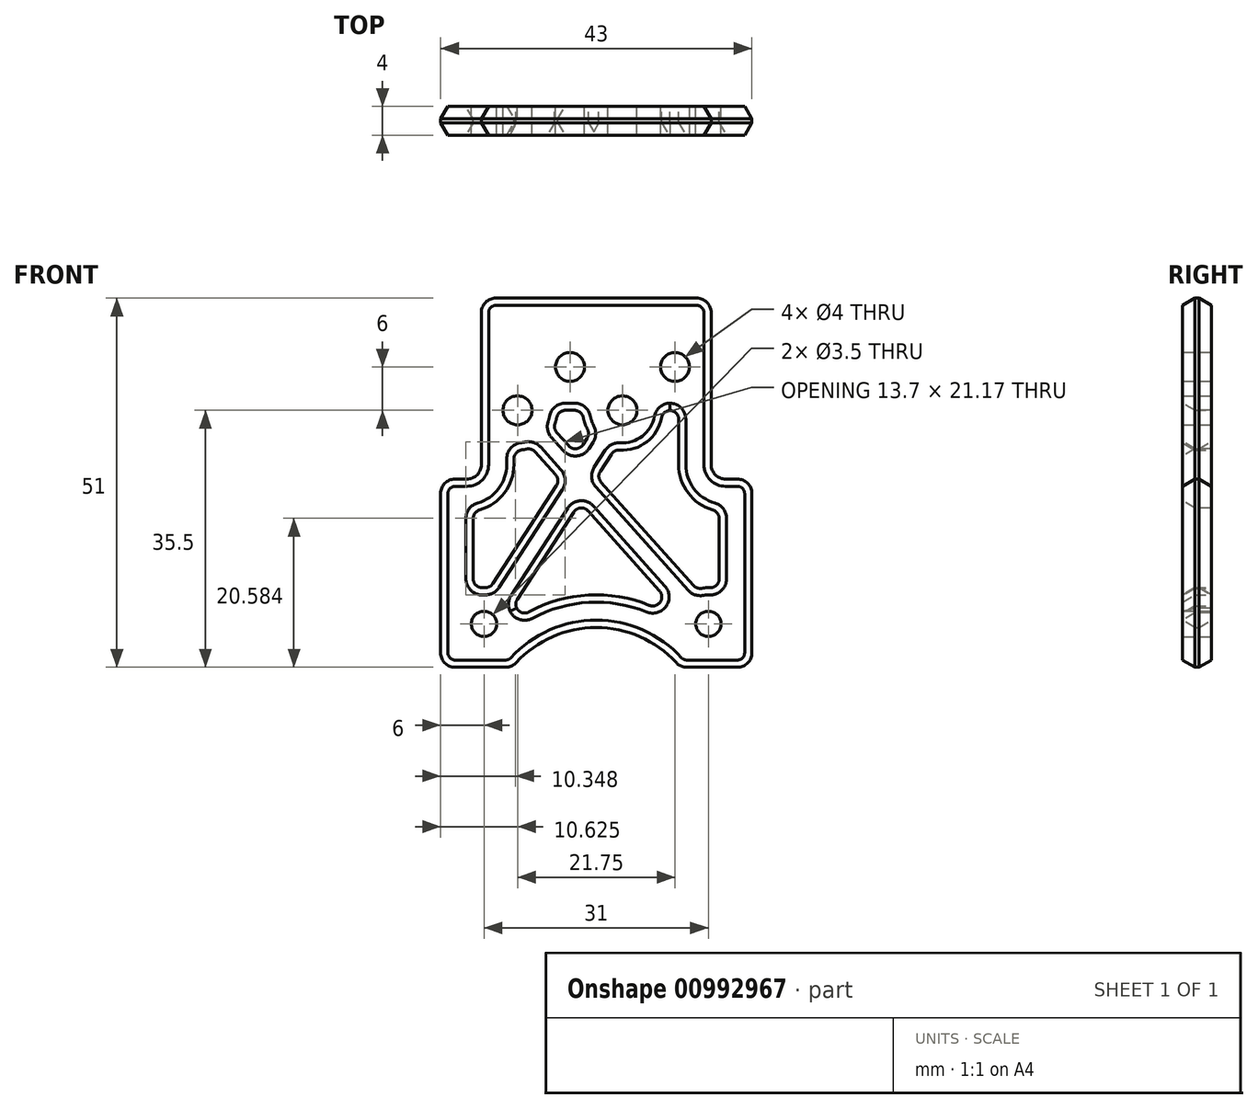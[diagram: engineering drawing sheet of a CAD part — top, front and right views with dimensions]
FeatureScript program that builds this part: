
annotation { "Feature Type Name" : "Feature", "Feature Type Description" : "" }
export const myFeature = defineFeature(function(context is Context, id is Id, definition is map)
    precondition{}
    {
        {
            var Q0;
            Q0=qCreatedBy(makeId("Front.planeOp"),FACE);
            var sketch = newSketch(context, id + "F0", { "sketchPlane" : qUnion([Q0])});
            skCircle(sketch, "E0", {"center": v(0, 0) * mm, "radius": 21.92 * mm, "construction": true});
            skLineSegment(sketch, "E1.bottom", {"start": v(-15.5, 15.5) * mm, "end": v(15.5, 15.5) * mm, "construction": true});
            skLineSegment(sketch, "E1.top", {"start": v(-15.5, -15.5) * mm, "end": v(15.5, -15.5) * mm, "construction": true});
            skLineSegment(sketch, "E1.left", {"start": v(-15.5, 15.5) * mm, "end": v(-15.5, -15.5) * mm, "construction": true});
            skLineSegment(sketch, "E1.right", {"start": v(15.5, 15.5) * mm, "end": v(15.5, -15.5) * mm, "construction": true});
            skCircle(sketch, "E2", {"center": v(-15.5, 15.5) * mm, "radius": 1.75 * mm});
            skCircle(sketch, "E3", {"center": v(15.5, 15.5) * mm, "radius": 1.75 * mm});
            skArc(sketch, "E4", {"start": v(11.6, 9.5) * mm, "mid": v(0, 15) * mm, "end": v(-11.6, 9.5) * mm});
            skLineSegment(sketch, "E5", {"start": v(-11.6, 9.5) * mm, "end": v(-21.5, 9.5) * mm});
            skLineSegment(sketch, "E6", {"start": v(-21.5, 9.5) * mm, "end": v(-21.5, 33.5) * mm});
            skLineSegment(sketch, "E7", {"start": v(-13.88, 60.5) * mm, "end": v(13.88, 60.5) * mm});
            skLineSegment(sketch, "E8", {"start": v(21.5, 33.5) * mm, "end": v(21.5, 9.5) * mm});
            skLineSegment(sketch, "E9", {"start": v(21.5, 9.5) * mm, "end": v(11.6, 9.5) * mm});
            skLineSegment(sketch, "E10", {"start": v(-21.5, 35.5) * mm, "end": v(21.5, 35.5) * mm, "construction": true});
            skPoint(sketch, "E10.endSnap0", {"position": v(21.5, 35) * mm});
            skLineSegment(sketch, "E11", {"start": v(15.88, 51) * mm, "end": v(-15.88, 51) * mm, "construction": true});
            skLineSegment(sketch, "E12", {"start": v(15.88, 45) * mm, "end": v(-15.88, 45) * mm, "construction": true});
            skLineSegment(sketch, "E13", {"start": v(15.88, 48) * mm, "end": v(-15.88, 48) * mm, "construction": true});
            skCircle(sketch, "E14", {"center": v(10.88, 51) * mm, "radius": 2 * mm});
            skCircle(sketch, "E15", {"center": v(3.63, 45) * mm, "radius": 2 * mm});
            skCircle(sketch, "E16", {"center": v(-10.88, 45) * mm, "radius": 2 * mm});
            skCircle(sketch, "E17", {"center": v(-3.62, 51) * mm, "radius": 2 * mm});
            skLineSegment(sketch, "E18", {"start": v(-3.63, 51) * mm, "end": v(3.63, 45) * mm, "construction": true});
            skLineSegment(sketch, "E19", {"start": v(0, -0.66) * mm, "end": v(0, 48) * mm, "construction": true});
            skLineSegment(sketch, "E20", {"start": v(-19.5, 35.5) * mm, "end": v(-15.87, 35.5) * mm});
            skLineSegment(sketch, "E21", {"start": v(-15.87, 35.5) * mm, "end": v(-15.88, 58.5) * mm});
            skLineSegment(sketch, "E22", {"start": v(19.5, 35.5) * mm, "end": v(15.88, 35.5) * mm});
            skLineSegment(sketch, "E23", {"start": v(15.88, 35.5) * mm, "end": v(15.88, 58.5) * mm});
            skPoint(sketch, "E24.orphan", {"position": v(21.5, 60.5) * mm});
            skCircle(sketch, "E25", {"center": v(-10.88, 45) * mm, "radius": 5 * mm, "construction": true});
            skCircle(sketch, "E26", {"center": v(10.88, 51) * mm, "radius": 5 * mm, "construction": true});
            skPoint(sketch, "E27.visualSharp", {"position": v(-21.5, 35.5) * mm});
            skArc(sketch, "E27.filletArc", {"start": v(-19.5, 35.5) * mm, "mid": v(-20.91, 34.91) * mm, "end": v(-21.5, 33.5) * mm});
            skPoint(sketch, "E28.visualSharp", {"position": v(21.5, 35.5) * mm});
            skArc(sketch, "E28.filletArc", {"start": v(21.5, 33.5) * mm, "mid": v(20.91, 34.91) * mm, "end": v(19.5, 35.5) * mm});
            skPoint(sketch, "E29.visualSharp", {"position": v(15.88, 60.5) * mm});
            skArc(sketch, "E29.filletArc", {"start": v(15.88, 58.5) * mm, "mid": v(15.29, 59.91) * mm, "end": v(13.88, 60.5) * mm});
            skPoint(sketch, "E30.visualSharp", {"position": v(-15.88, 60.5) * mm});
            skArc(sketch, "E30.filletArc", {"start": v(-13.88, 60.5) * mm, "mid": v(-15.29, 59.91) * mm, "end": v(-15.88, 58.5) * mm});
            skSolve(sketch);
        }
        {
            var Q0;
            Q0 = qSketchRegion(id + "F0", true);
            extrude(context, id + "F1", {"entities" : qUnion([Q0]), "depth" : 4 * mm, "offsetDistance" : 25 * mm});
        }
        {
            var Q0;
            Q0=makeQuery(id+"F1.opExtrude","SWEPT_EDGE",EDGE,{"disambiguationData":[OSD([sQuery(id+"F0.wireOp",EDGE,"E22"),sQuery(id+"F0.wireOp",EDGE,"E23")])]});
            var Q1;
            Q1=makeQuery(id+"F1.opExtrude","SWEPT_EDGE",EDGE,{"disambiguationData":[OSD([sQuery(id+"F0.wireOp",EDGE,"E20"),sQuery(id+"F0.wireOp",EDGE,"E21")])]});
            var Q2;
            Q2=makeQuery(id+"F1.opExtrude","SWEPT_EDGE",EDGE,{"disambiguationData":[OSD([sQuery(id+"F0.wireOp",EDGE,"E4"),sQuery(id+"F0.wireOp",EDGE,"E9")])]});
            var Q3;
            Q3=makeQuery(id+"F1.opExtrude","SWEPT_EDGE",EDGE,{"disambiguationData":[OSD([sQuery(id+"F0.wireOp",EDGE,"E8"),sQuery(id+"F0.wireOp",EDGE,"E9")])]});
            var Q4;
            Q4=makeQuery(id+"F1.opExtrude","SWEPT_EDGE",EDGE,{"disambiguationData":[OSD([sQuery(id+"F0.wireOp",EDGE,"E4"),sQuery(id+"F0.wireOp",EDGE,"E5")])]});
            var Q5;
            Q5=makeQuery(id+"F1.opExtrude","SWEPT_EDGE",EDGE,{"disambiguationData":[OSD([sQuery(id+"F0.wireOp",EDGE,"E5"),sQuery(id+"F0.wireOp",EDGE,"E6")])]});
            fillet(context, id + "F2", {"entities" : qUnion([Q0, Q1, Q2, Q3, Q4, Q5]), "radius" : 2 * mm, "tangentPropagation" : true, "allowEdgeOverflow" : false});
        }
        {
            var Q0;
            Q0=makeQuery(id+"F1.opExtrude","CAP_EDGE",EDGE,{"disambiguationData":[OSD([sQuery(id+"F0.wireOp",EDGE,"E8")])],"isStart":true});
            var Q1;
            Q1=makeQuery(id+"F1.opExtrude","CAP_EDGE",EDGE,{"disambiguationData":[OSD([sQuery(id+"F0.wireOp",EDGE,"E8")])],"isStart":false});
            chamfer(context, id + "F3", {"entities" : qUnion([Q0, Q1]), "chamferType" : ChamferType.OFFSET_ANGLE, "width" : 1 * mm, "oppositeDirection" : false, "angle" : 60 * degree, "tangentPropagation" : true});
        }
        {
            var Q0;
            Q0=makeQuery(id+"F1.opExtrude","CAP_FACE",FACE,{"disambiguationData":[OSD([sQuery(id+"F0.wireOp",EDGE,"E2"),sQuery(id+"F0.wireOp",EDGE,"E3"),sQuery(id+"F0.wireOp",EDGE,"E4"),sQuery(id+"F0.wireOp",EDGE,"E5"),sQuery(id+"F0.wireOp",EDGE,"E6"),sQuery(id+"F0.wireOp",EDGE,"E7"),sQuery(id+"F0.wireOp",EDGE,"E8"),sQuery(id+"F0.wireOp",EDGE,"E9"),sQuery(id+"F0.wireOp",EDGE,"E14"),sQuery(id+"F0.wireOp",EDGE,"E15"),sQuery(id+"F0.wireOp",EDGE,"E16"),sQuery(id+"F0.wireOp",EDGE,"E17"),sQuery(id+"F0.wireOp",EDGE,"E20"),sQuery(id+"F0.wireOp",EDGE,"E21"),sQuery(id+"F0.wireOp",EDGE,"E22"),sQuery(id+"F0.wireOp",EDGE,"E23"),sQuery(id+"F0.wireOp",EDGE,"E27.filletArc"),sQuery(id+"F0.wireOp",EDGE,"E28.filletArc"),sQuery(id+"F0.wireOp",EDGE,"E29.filletArc"),sQuery(id+"F0.wireOp",EDGE,"E30.filletArc")])],"isStart":true});
            var sketch = newSketch(context, id + "F4", { "sketchPlane" : qUnion([Q0])});
            skArc(sketch, "E31", {"start": v(-10.58, 16.38) * mm, "mid": v(-10.73, 17) * mm, "end": v(-10.95, 17.58) * mm});
            skArc(sketch, "E32", {"start": v(17, 20.27) * mm, "mid": v(15.85, 20.49) * mm, "end": v(14.69, 20.43) * mm});
            skLineSegment(sketch, "E33.0", {"start": v(11.37, 37.5) * mm, "end": v(11.37, 39.52) * mm});
            skArc(sketch, "E33.1", {"start": v(17, 31.06) * mm, "mid": v(12.98, 33.22) * mm, "end": v(11.37, 37.5) * mm});
            skLineSegment(sketch, "E33.2", {"start": v(17, 20.27) * mm, "end": v(17, 31.06) * mm});
            skArc(sketch, "E33.4", {"start": v(-10.58, 16.38) * mm, "mid": v(0, 19.5) * mm, "end": v(10.58, 16.38) * mm});
            skLineSegment(sketch, "E33.5", {"start": v(-11.37, 45) * mm, "end": v(-11.37, 37.5) * mm});
            skArc(sketch, "E33.6", {"start": v(-11.37, 37.5) * mm, "mid": v(-12.98, 33.22) * mm, "end": v(-17, 31.06) * mm});
            skLineSegment(sketch, "E33.7", {"start": v(-17, 31.06) * mm, "end": v(-17, 20.27) * mm});
            skArc(sketch, "E34.0", {"start": v(-9.13, 45) * mm, "mid": v(-7.1, 40.74) * mm, "end": v(-2.52, 39.61) * mm});
            skArc(sketch, "E35.0", {"start": v(5.38, 45) * mm, "mid": v(5.53, 43.72) * mm, "end": v(5.97, 42.51) * mm});
            skLineSegment(sketch, "E36", {"start": v(-11.37, 45) * mm, "end": v(-9.13, 45) * mm});
            skLineSegment(sketch, "E37.trimOffspring", {"start": v(1.87, 45) * mm, "end": v(5.38, 45) * mm});
            skLineSegment(sketch, "E38", {"start": v(-15.5, 15.5) * mm, "end": v(10.88, 45) * mm, "construction": true});
            skLineSegment(sketch, "E39", {"start": v(-3.63, 45) * mm, "end": v(15.5, 15.5) * mm, "construction": true});
            skLineSegment(sketch, "E40.0", {"start": v(-10.95, 17.58) * mm, "end": v(2.22, 32.31) * mm});
            skLineSegment(sketch, "E41.0", {"start": v(-13.94, 20.25) * mm, "end": v(-0.04, 35.8) * mm});
            skArc(sketch, "E42.trimOffspring", {"start": v(-13.94, 20.25) * mm, "mid": v(-15.47, 20.5) * mm, "end": v(-17, 20.27) * mm});
            skArc(sketch, "E43.trimOffspring", {"start": v(8.95, 39.85) * mm, "mid": v(10.14, 39.55) * mm, "end": v(11.37, 39.52) * mm});
            skLineSegment(sketch, "E44.0", {"start": v(-2.52, 39.61) * mm, "end": v(-0.04, 35.8) * mm});
            skLineSegment(sketch, "E45.0", {"start": v(0.84, 41.79) * mm, "end": v(2.72, 38.88) * mm});
            skArc(sketch, "E46.trimOffspring", {"start": v(0.84, 41.79) * mm, "mid": v(1.6, 43.31) * mm, "end": v(1.87, 45) * mm});
            skLineSegment(sketch, "E47.trimOffspring", {"start": v(2.72, 38.88) * mm, "end": v(5.97, 42.51) * mm});
            skLineSegment(sketch, "E48.trimOffspring", {"start": v(2.22, 32.31) * mm, "end": v(11.33, 18.26) * mm});
            skLineSegment(sketch, "E49.trimOffspring", {"start": v(4.98, 35.4) * mm, "end": v(8.95, 39.85) * mm});
            skLineSegment(sketch, "E50.trimOffspring", {"start": v(4.98, 35.4) * mm, "end": v(14.69, 20.43) * mm});
            skArc(sketch, "E51.trimOffspring", {"start": v(11.33, 18.26) * mm, "mid": v(10.86, 17.36) * mm, "end": v(10.58, 16.38) * mm});
            skSolve(sketch);
        }
        {
            var Q0;
            Q0 = qSketchRegion(id + "F4", true);
            extrude(context, id + "F5", {"entities" : qUnion([Q0]), "operationType" : NewBodyOperationType.REMOVE, "oppositeDirection" : true, "depth" : 25 * mm, "offsetDistance" : 25 * mm});
        }
        {
            var Q0;
            Q0=makeQuery(id+"F5.boolean.opBoolean","COPY",EDGE,{"derivedFrom":makeQuery(id+"F5.opExtrude","SWEPT_EDGE",EDGE,{"disambiguationData":[OSD([sQuery(id+"F4.wireOp",EDGE,"E33.5"),sQuery(id+"F4.wireOp",EDGE,"E36")])]})});
            var Q1;
            Q1=makeQuery(id+"F5.boolean.opBoolean","COPY",EDGE,{"derivedFrom":makeQuery(id+"F5.opExtrude","SWEPT_EDGE",EDGE,{"disambiguationData":[OSD([sQuery(id+"F4.wireOp",EDGE,"E34.0"),sQuery(id+"F4.wireOp",EDGE,"E36")])]})});
            var Q2;
            Q2=makeQuery(id+"F5.boolean.opBoolean","COPY",EDGE,{"derivedFrom":makeQuery(id+"F5.opExtrude","SWEPT_EDGE",EDGE,{"disambiguationData":[OSD([sQuery(id+"F4.wireOp",EDGE,"E37.trimOffspring"),sQuery(id+"F4.wireOp",EDGE,"E46.trimOffspring")])]})});
            var Q3;
            Q3=makeQuery(id+"F5.boolean.opBoolean","COPY",EDGE,{"derivedFrom":makeQuery(id+"F5.opExtrude","SWEPT_EDGE",EDGE,{"disambiguationData":[OSD([sQuery(id+"F4.wireOp",EDGE,"E35.0"),sQuery(id+"F4.wireOp",EDGE,"E37.trimOffspring")])]})});
            var Q4;
            Q4=makeQuery(id+"F5.boolean.opBoolean","COPY",EDGE,{"derivedFrom":makeQuery(id+"F5.opExtrude","SWEPT_EDGE",EDGE,{"disambiguationData":[OSD([sQuery(id+"F4.wireOp",EDGE,"E33.0"),sQuery(id+"F4.wireOp",EDGE,"E43.trimOffspring")])]})});
            var Q5;
            Q5=makeQuery(id+"F5.boolean.opBoolean","COPY",EDGE,{"derivedFrom":makeQuery(id+"F5.opExtrude","SWEPT_EDGE",EDGE,{"disambiguationData":[OSD([sQuery(id+"F4.wireOp",EDGE,"E43.trimOffspring"),sQuery(id+"F4.wireOp",EDGE,"E49.trimOffspring")])]})});
            var Q6;
            Q6=makeQuery(id+"F5.boolean.opBoolean","COPY",EDGE,{"derivedFrom":makeQuery(id+"F5.opExtrude","SWEPT_EDGE",EDGE,{"disambiguationData":[OSD([sQuery(id+"F4.wireOp",EDGE,"E35.0"),sQuery(id+"F4.wireOp",EDGE,"E47.trimOffspring")])]})});
            var Q7;
            Q7=makeQuery(id+"F5.boolean.opBoolean","COPY",EDGE,{"derivedFrom":makeQuery(id+"F5.opExtrude","SWEPT_EDGE",EDGE,{"disambiguationData":[OSD([sQuery(id+"F4.wireOp",EDGE,"E45.0"),sQuery(id+"F4.wireOp",EDGE,"E47.trimOffspring")])]})});
            var Q8;
            Q8=makeQuery(id+"F5.boolean.opBoolean","COPY",EDGE,{"derivedFrom":makeQuery(id+"F5.opExtrude","SWEPT_EDGE",EDGE,{"disambiguationData":[OSD([sQuery(id+"F4.wireOp",EDGE,"E45.0"),sQuery(id+"F4.wireOp",EDGE,"E46.trimOffspring")])]})});
            var Q9;
            Q9=makeQuery(id+"F5.boolean.opBoolean","COPY",EDGE,{"derivedFrom":makeQuery(id+"F5.opExtrude","SWEPT_EDGE",EDGE,{"disambiguationData":[OSD([sQuery(id+"F4.wireOp",EDGE,"E49.trimOffspring"),sQuery(id+"F4.wireOp",EDGE,"E50.trimOffspring")])]})});
            var Q10;
            Q10=makeQuery(id+"F5.boolean.opBoolean","COPY",EDGE,{"derivedFrom":makeQuery(id+"F5.opExtrude","SWEPT_EDGE",EDGE,{"disambiguationData":[OSD([sQuery(id+"F4.wireOp",EDGE,"E34.0"),sQuery(id+"F4.wireOp",EDGE,"E44.0")])]})});
            var Q11;
            Q11=makeQuery(id+"F5.boolean.opBoolean","COPY",EDGE,{"derivedFrom":makeQuery(id+"F5.opExtrude","SWEPT_EDGE",EDGE,{"disambiguationData":[OSD([sQuery(id+"F4.wireOp",EDGE,"E41.0"),sQuery(id+"F4.wireOp",EDGE,"E44.0")])]})});
            var Q12;
            Q12=makeQuery(id+"F5.boolean.opBoolean","COPY",EDGE,{"derivedFrom":makeQuery(id+"F5.opExtrude","SWEPT_EDGE",EDGE,{"disambiguationData":[OSD([sQuery(id+"F4.wireOp",EDGE,"E33.1"),sQuery(id+"F4.wireOp",EDGE,"E33.2")])]})});
            var Q13;
            Q13=makeQuery(id+"F5.boolean.opBoolean","COPY",EDGE,{"derivedFrom":makeQuery(id+"F5.opExtrude","SWEPT_EDGE",EDGE,{"disambiguationData":[OSD([sQuery(id+"F4.wireOp",EDGE,"E40.0"),sQuery(id+"F4.wireOp",EDGE,"E48.trimOffspring")])]})});
            var Q14;
            Q14=makeQuery(id+"F5.boolean.opBoolean","COPY",EDGE,{"derivedFrom":makeQuery(id+"F5.opExtrude","SWEPT_EDGE",EDGE,{"disambiguationData":[OSD([sQuery(id+"F4.wireOp",EDGE,"E33.6"),sQuery(id+"F4.wireOp",EDGE,"E33.7")])]})});
            var Q15;
            Q15=makeQuery(id+"F5.boolean.opBoolean","COPY",EDGE,{"derivedFrom":makeQuery(id+"F5.opExtrude","SWEPT_EDGE",EDGE,{"disambiguationData":[OSD([sQuery(id+"F4.wireOp",EDGE,"E33.7"),sQuery(id+"F4.wireOp",EDGE,"E42.trimOffspring")])]})});
            var Q16;
            Q16=makeQuery(id+"F5.boolean.opBoolean","COPY",EDGE,{"derivedFrom":makeQuery(id+"F5.opExtrude","SWEPT_EDGE",EDGE,{"disambiguationData":[OSD([sQuery(id+"F4.wireOp",EDGE,"E41.0"),sQuery(id+"F4.wireOp",EDGE,"E42.trimOffspring")])]})});
            var Q17;
            Q17=makeQuery(id+"F5.boolean.opBoolean","COPY",EDGE,{"derivedFrom":makeQuery(id+"F5.opExtrude","SWEPT_EDGE",EDGE,{"disambiguationData":[OSD([sQuery(id+"F4.wireOp",EDGE,"E31"),sQuery(id+"F4.wireOp",EDGE,"E33.4")])]})});
            var Q18;
            Q18=makeQuery(id+"F5.boolean.opBoolean","COPY",EDGE,{"derivedFrom":makeQuery(id+"F5.opExtrude","SWEPT_EDGE",EDGE,{"disambiguationData":[OSD([sQuery(id+"F4.wireOp",EDGE,"E33.4"),sQuery(id+"F4.wireOp",EDGE,"E51.trimOffspring")])]})});
            var Q19;
            Q19=makeQuery(id+"F5.boolean.opBoolean","COPY",EDGE,{"derivedFrom":makeQuery(id+"F5.opExtrude","SWEPT_EDGE",EDGE,{"disambiguationData":[OSD([sQuery(id+"F4.wireOp",EDGE,"E48.trimOffspring"),sQuery(id+"F4.wireOp",EDGE,"E51.trimOffspring")])]})});
            var Q20;
            Q20=makeQuery(id+"F5.boolean.opBoolean","COPY",EDGE,{"derivedFrom":makeQuery(id+"F5.opExtrude","SWEPT_EDGE",EDGE,{"disambiguationData":[OSD([sQuery(id+"F4.wireOp",EDGE,"E32"),sQuery(id+"F4.wireOp",EDGE,"E50.trimOffspring")])]})});
            var Q21;
            Q21=makeQuery(id+"F5.boolean.opBoolean","COPY",EDGE,{"derivedFrom":makeQuery(id+"F5.opExtrude","SWEPT_EDGE",EDGE,{"disambiguationData":[OSD([sQuery(id+"F4.wireOp",EDGE,"E32"),sQuery(id+"F4.wireOp",EDGE,"E33.2")])]})});
            fillet(context, id + "F6", {"entities" : qUnion([Q0, Q1, Q2, Q3, Q4, Q5, Q6, Q7, Q8, Q9, Q10, Q11, Q12, Q13, Q14, Q15, Q16, Q17, Q18, Q19, Q20, Q21]), "radius" : 1.25 * mm, "tangentPropagation" : true, "allowEdgeOverflow" : false});
        }
        {
            var Q0;
            Q0=makeQuery(id+"F6.opFillet","BLEND_EDGE",EDGE,{"blendedFrom":[makeQuery(id+"F5.boolean.opBoolean","COPY",EDGE,{"derivedFrom":makeQuery(id+"F5.opExtrude","SWEPT_EDGE",EDGE,{"disambiguationData":[OSD([sQuery(id+"F4.wireOp",EDGE,"E31"),sQuery(id+"F4.wireOp",EDGE,"E33.4")])]})}),makeQuery(id+"F5.boolean.opBoolean","COPY",FACE,{"derivedFrom":makeQuery(id+"F5.opExtrude","SWEPT_FACE",FACE,{"disambiguationData":[OSD([sQuery(id+"F4.wireOp",EDGE,"E40.0")])]})})],"blendedInto":[makeQuery(id+"F5.boolean.opBoolean","COPY",FACE,{"derivedFrom":makeQuery(id+"F5.opExtrude","SWEPT_FACE",FACE,{"disambiguationData":[OSD([sQuery(id+"F4.wireOp",EDGE,"E40.0")])]})})]});
            fillet(context, id + "F7", {"entities" : qUnion([Q0]), "radius" : 1.25 * mm, "tangentPropagation" : true, "allowEdgeOverflow" : false});
        }
        {
            var Q0;
            Q0=makeQuery(id+"F5.boolean.opBoolean","INTERSECT",EDGE,{"derivedFrom":[makeQuery(id+"F1.opExtrude","CAP_FACE",FACE,{"disambiguationData":[OSD([sQuery(id+"F0.wireOp",EDGE,"E2"),sQuery(id+"F0.wireOp",EDGE,"E3"),sQuery(id+"F0.wireOp",EDGE,"E4"),sQuery(id+"F0.wireOp",EDGE,"E5"),sQuery(id+"F0.wireOp",EDGE,"E6"),sQuery(id+"F0.wireOp",EDGE,"E7"),sQuery(id+"F0.wireOp",EDGE,"E8"),sQuery(id+"F0.wireOp",EDGE,"E9"),sQuery(id+"F0.wireOp",EDGE,"E14"),sQuery(id+"F0.wireOp",EDGE,"E15"),sQuery(id+"F0.wireOp",EDGE,"E16"),sQuery(id+"F0.wireOp",EDGE,"E17"),sQuery(id+"F0.wireOp",EDGE,"E20"),sQuery(id+"F0.wireOp",EDGE,"E21"),sQuery(id+"F0.wireOp",EDGE,"E22"),sQuery(id+"F0.wireOp",EDGE,"E23"),sQuery(id+"F0.wireOp",EDGE,"E27.filletArc"),sQuery(id+"F0.wireOp",EDGE,"E28.filletArc"),sQuery(id+"F0.wireOp",EDGE,"E29.filletArc"),sQuery(id+"F0.wireOp",EDGE,"E30.filletArc")])],"isStart":false}),makeQuery(id+"F5.opExtrude","SWEPT_FACE",FACE,{"disambiguationData":[OSD([sQuery(id+"F4.wireOp",EDGE,"E48.trimOffspring")])]})]});
            var Q1;
            Q1=makeQuery(id+"F5.boolean.opBoolean","INTERSECT",EDGE,{"derivedFrom":[makeQuery(id+"F1.opExtrude","CAP_FACE",FACE,{"disambiguationData":[OSD([sQuery(id+"F0.wireOp",EDGE,"E2"),sQuery(id+"F0.wireOp",EDGE,"E3"),sQuery(id+"F0.wireOp",EDGE,"E4"),sQuery(id+"F0.wireOp",EDGE,"E5"),sQuery(id+"F0.wireOp",EDGE,"E6"),sQuery(id+"F0.wireOp",EDGE,"E7"),sQuery(id+"F0.wireOp",EDGE,"E8"),sQuery(id+"F0.wireOp",EDGE,"E9"),sQuery(id+"F0.wireOp",EDGE,"E14"),sQuery(id+"F0.wireOp",EDGE,"E15"),sQuery(id+"F0.wireOp",EDGE,"E16"),sQuery(id+"F0.wireOp",EDGE,"E17"),sQuery(id+"F0.wireOp",EDGE,"E20"),sQuery(id+"F0.wireOp",EDGE,"E21"),sQuery(id+"F0.wireOp",EDGE,"E22"),sQuery(id+"F0.wireOp",EDGE,"E23"),sQuery(id+"F0.wireOp",EDGE,"E27.filletArc"),sQuery(id+"F0.wireOp",EDGE,"E28.filletArc"),sQuery(id+"F0.wireOp",EDGE,"E29.filletArc"),sQuery(id+"F0.wireOp",EDGE,"E30.filletArc")])],"isStart":false}),makeQuery(id+"F5.opExtrude","SWEPT_FACE",FACE,{"disambiguationData":[OSD([sQuery(id+"F4.wireOp",EDGE,"E33.1")])]})]});
            var Q2;
            Q2=makeQuery(id+"F6.opFillet","BLEND_EDGE",EDGE,{"blendedFrom":[makeQuery(id+"F5.boolean.opBoolean","COPY",EDGE,{"derivedFrom":makeQuery(id+"F5.opExtrude","SWEPT_EDGE",EDGE,{"disambiguationData":[OSD([sQuery(id+"F4.wireOp",EDGE,"E34.0"),sQuery(id+"F4.wireOp",EDGE,"E44.0")])]})}),makeQuery(id+"F1.opExtrude","CAP_FACE",FACE,{"disambiguationData":[OSD([sQuery(id+"F0.wireOp",EDGE,"E2"),sQuery(id+"F0.wireOp",EDGE,"E3"),sQuery(id+"F0.wireOp",EDGE,"E4"),sQuery(id+"F0.wireOp",EDGE,"E5"),sQuery(id+"F0.wireOp",EDGE,"E6"),sQuery(id+"F0.wireOp",EDGE,"E7"),sQuery(id+"F0.wireOp",EDGE,"E8"),sQuery(id+"F0.wireOp",EDGE,"E9"),sQuery(id+"F0.wireOp",EDGE,"E14"),sQuery(id+"F0.wireOp",EDGE,"E15"),sQuery(id+"F0.wireOp",EDGE,"E16"),sQuery(id+"F0.wireOp",EDGE,"E17"),sQuery(id+"F0.wireOp",EDGE,"E20"),sQuery(id+"F0.wireOp",EDGE,"E21"),sQuery(id+"F0.wireOp",EDGE,"E22"),sQuery(id+"F0.wireOp",EDGE,"E23"),sQuery(id+"F0.wireOp",EDGE,"E27.filletArc"),sQuery(id+"F0.wireOp",EDGE,"E28.filletArc"),sQuery(id+"F0.wireOp",EDGE,"E29.filletArc"),sQuery(id+"F0.wireOp",EDGE,"E30.filletArc")])],"isStart":false})],"blendedInto":[makeQuery(id+"F1.opExtrude","CAP_FACE",FACE,{"disambiguationData":[OSD([sQuery(id+"F0.wireOp",EDGE,"E2"),sQuery(id+"F0.wireOp",EDGE,"E3"),sQuery(id+"F0.wireOp",EDGE,"E4"),sQuery(id+"F0.wireOp",EDGE,"E5"),sQuery(id+"F0.wireOp",EDGE,"E6"),sQuery(id+"F0.wireOp",EDGE,"E7"),sQuery(id+"F0.wireOp",EDGE,"E8"),sQuery(id+"F0.wireOp",EDGE,"E9"),sQuery(id+"F0.wireOp",EDGE,"E14"),sQuery(id+"F0.wireOp",EDGE,"E15"),sQuery(id+"F0.wireOp",EDGE,"E16"),sQuery(id+"F0.wireOp",EDGE,"E17"),sQuery(id+"F0.wireOp",EDGE,"E20"),sQuery(id+"F0.wireOp",EDGE,"E21"),sQuery(id+"F0.wireOp",EDGE,"E22"),sQuery(id+"F0.wireOp",EDGE,"E23"),sQuery(id+"F0.wireOp",EDGE,"E27.filletArc"),sQuery(id+"F0.wireOp",EDGE,"E28.filletArc"),sQuery(id+"F0.wireOp",EDGE,"E29.filletArc"),sQuery(id+"F0.wireOp",EDGE,"E30.filletArc")])],"isStart":false})]});
            var Q3;
            Q3=makeQuery(id+"F5.boolean.opBoolean","COPY",EDGE,{"derivedFrom":makeQuery(id+"F5.opExtrude","CAP_EDGE",EDGE,{"disambiguationData":[OSD([sQuery(id+"F4.wireOp",EDGE,"E33.6")])],"isStart":true})});
            var Q4;
            Q4=makeQuery(id+"F5.boolean.opBoolean","COPY",EDGE,{"derivedFrom":makeQuery(id+"F5.opExtrude","CAP_EDGE",EDGE,{"disambiguationData":[OSD([sQuery(id+"F4.wireOp",EDGE,"E40.0")])],"isStart":true})});
            var Q5;
            Q5=makeQuery(id+"F6.opFillet","BLEND_EDGE",EDGE,{"blendedFrom":[makeQuery(id+"F5.boolean.opBoolean","COPY",EDGE,{"derivedFrom":makeQuery(id+"F5.opExtrude","SWEPT_EDGE",EDGE,{"disambiguationData":[OSD([sQuery(id+"F4.wireOp",EDGE,"E49.trimOffspring"),sQuery(id+"F4.wireOp",EDGE,"E50.trimOffspring")])]})}),makeQuery(id+"F1.opExtrude","CAP_FACE",FACE,{"disambiguationData":[OSD([sQuery(id+"F0.wireOp",EDGE,"E2"),sQuery(id+"F0.wireOp",EDGE,"E3"),sQuery(id+"F0.wireOp",EDGE,"E4"),sQuery(id+"F0.wireOp",EDGE,"E5"),sQuery(id+"F0.wireOp",EDGE,"E6"),sQuery(id+"F0.wireOp",EDGE,"E7"),sQuery(id+"F0.wireOp",EDGE,"E8"),sQuery(id+"F0.wireOp",EDGE,"E9"),sQuery(id+"F0.wireOp",EDGE,"E14"),sQuery(id+"F0.wireOp",EDGE,"E15"),sQuery(id+"F0.wireOp",EDGE,"E16"),sQuery(id+"F0.wireOp",EDGE,"E17"),sQuery(id+"F0.wireOp",EDGE,"E20"),sQuery(id+"F0.wireOp",EDGE,"E21"),sQuery(id+"F0.wireOp",EDGE,"E22"),sQuery(id+"F0.wireOp",EDGE,"E23"),sQuery(id+"F0.wireOp",EDGE,"E27.filletArc"),sQuery(id+"F0.wireOp",EDGE,"E28.filletArc"),sQuery(id+"F0.wireOp",EDGE,"E29.filletArc"),sQuery(id+"F0.wireOp",EDGE,"E30.filletArc")])],"isStart":true})],"blendedInto":[makeQuery(id+"F1.opExtrude","CAP_FACE",FACE,{"disambiguationData":[OSD([sQuery(id+"F0.wireOp",EDGE,"E2"),sQuery(id+"F0.wireOp",EDGE,"E3"),sQuery(id+"F0.wireOp",EDGE,"E4"),sQuery(id+"F0.wireOp",EDGE,"E5"),sQuery(id+"F0.wireOp",EDGE,"E6"),sQuery(id+"F0.wireOp",EDGE,"E7"),sQuery(id+"F0.wireOp",EDGE,"E8"),sQuery(id+"F0.wireOp",EDGE,"E9"),sQuery(id+"F0.wireOp",EDGE,"E14"),sQuery(id+"F0.wireOp",EDGE,"E15"),sQuery(id+"F0.wireOp",EDGE,"E16"),sQuery(id+"F0.wireOp",EDGE,"E17"),sQuery(id+"F0.wireOp",EDGE,"E20"),sQuery(id+"F0.wireOp",EDGE,"E21"),sQuery(id+"F0.wireOp",EDGE,"E22"),sQuery(id+"F0.wireOp",EDGE,"E23"),sQuery(id+"F0.wireOp",EDGE,"E27.filletArc"),sQuery(id+"F0.wireOp",EDGE,"E28.filletArc"),sQuery(id+"F0.wireOp",EDGE,"E29.filletArc"),sQuery(id+"F0.wireOp",EDGE,"E30.filletArc")])],"isStart":true})]});
            var Q6;
            Q6=makeQuery(id+"F5.boolean.opBoolean","COPY",EDGE,{"derivedFrom":makeQuery(id+"F5.opExtrude","CAP_EDGE",EDGE,{"disambiguationData":[OSD([sQuery(id+"F4.wireOp",EDGE,"E46.trimOffspring")])],"isStart":true})});
            var Q7;
            Q7=makeQuery(id+"F6.opFillet","BLEND_EDGE",EDGE,{"blendedFrom":[makeQuery(id+"F5.boolean.opBoolean","COPY",EDGE,{"derivedFrom":makeQuery(id+"F5.opExtrude","SWEPT_EDGE",EDGE,{"disambiguationData":[OSD([sQuery(id+"F4.wireOp",EDGE,"E37.trimOffspring"),sQuery(id+"F4.wireOp",EDGE,"E46.trimOffspring")])]})}),makeQuery(id+"F1.opExtrude","CAP_FACE",FACE,{"disambiguationData":[OSD([sQuery(id+"F0.wireOp",EDGE,"E2"),sQuery(id+"F0.wireOp",EDGE,"E3"),sQuery(id+"F0.wireOp",EDGE,"E4"),sQuery(id+"F0.wireOp",EDGE,"E5"),sQuery(id+"F0.wireOp",EDGE,"E6"),sQuery(id+"F0.wireOp",EDGE,"E7"),sQuery(id+"F0.wireOp",EDGE,"E8"),sQuery(id+"F0.wireOp",EDGE,"E9"),sQuery(id+"F0.wireOp",EDGE,"E14"),sQuery(id+"F0.wireOp",EDGE,"E15"),sQuery(id+"F0.wireOp",EDGE,"E16"),sQuery(id+"F0.wireOp",EDGE,"E17"),sQuery(id+"F0.wireOp",EDGE,"E20"),sQuery(id+"F0.wireOp",EDGE,"E21"),sQuery(id+"F0.wireOp",EDGE,"E22"),sQuery(id+"F0.wireOp",EDGE,"E23"),sQuery(id+"F0.wireOp",EDGE,"E27.filletArc"),sQuery(id+"F0.wireOp",EDGE,"E28.filletArc"),sQuery(id+"F0.wireOp",EDGE,"E29.filletArc"),sQuery(id+"F0.wireOp",EDGE,"E30.filletArc")])],"isStart":false})],"blendedInto":[makeQuery(id+"F1.opExtrude","CAP_FACE",FACE,{"disambiguationData":[OSD([sQuery(id+"F0.wireOp",EDGE,"E2"),sQuery(id+"F0.wireOp",EDGE,"E3"),sQuery(id+"F0.wireOp",EDGE,"E4"),sQuery(id+"F0.wireOp",EDGE,"E5"),sQuery(id+"F0.wireOp",EDGE,"E6"),sQuery(id+"F0.wireOp",EDGE,"E7"),sQuery(id+"F0.wireOp",EDGE,"E8"),sQuery(id+"F0.wireOp",EDGE,"E9"),sQuery(id+"F0.wireOp",EDGE,"E14"),sQuery(id+"F0.wireOp",EDGE,"E15"),sQuery(id+"F0.wireOp",EDGE,"E16"),sQuery(id+"F0.wireOp",EDGE,"E17"),sQuery(id+"F0.wireOp",EDGE,"E20"),sQuery(id+"F0.wireOp",EDGE,"E21"),sQuery(id+"F0.wireOp",EDGE,"E22"),sQuery(id+"F0.wireOp",EDGE,"E23"),sQuery(id+"F0.wireOp",EDGE,"E27.filletArc"),sQuery(id+"F0.wireOp",EDGE,"E28.filletArc"),sQuery(id+"F0.wireOp",EDGE,"E29.filletArc"),sQuery(id+"F0.wireOp",EDGE,"E30.filletArc")])],"isStart":false})]});
            chamfer(context, id + "F8", {"entities" : qUnion([Q0, Q1, Q2, Q3, Q4, Q5, Q6, Q7]), "chamferType" : ChamferType.OFFSET_ANGLE, "width" : 1 * mm, "oppositeDirection" : false, "angle" : 60 * degree, "tangentPropagation" : true});
        }
    });
